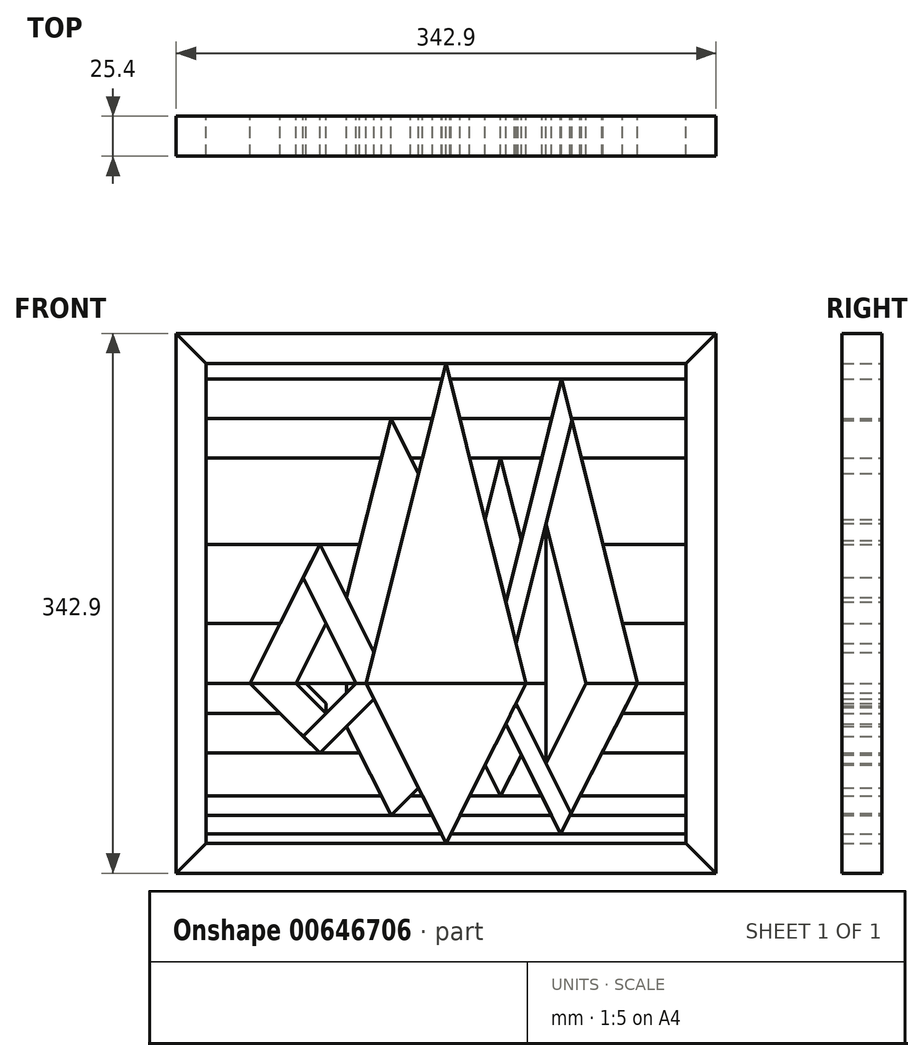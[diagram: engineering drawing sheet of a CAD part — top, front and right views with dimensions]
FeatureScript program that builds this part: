
annotation { "Feature Type Name" : "Feature", "Feature Type Description" : "" }
export const myFeature = defineFeature(function(context is Context, id is Id, definition is map)
    precondition{}
    {
        {
            var Q0;
            Q0=qCreatedBy(makeId("Front.planeOp"),FACE);
            var sketch = newSketch(context, id + "F0", { "sketchPlane" : qUnion([Q0])});
            skLineSegment(sketch, "E0.bottom", {"start": v(152.4, -152.4) * mm, "end": v(-152.4, -152.4) * mm});
            skLineSegment(sketch, "E0.top", {"start": v(152.4, 152.4) * mm, "end": v(-152.4, 152.4) * mm});
            skLineSegment(sketch, "E0.left", {"start": v(152.4, -152.4) * mm, "end": v(152.4, 152.4) * mm});
            skLineSegment(sketch, "E0.right", {"start": v(-152.4, -152.4) * mm, "end": v(-152.4, 152.4) * mm});
            skPoint(sketch, "E0.middle", {"position": v(0, 0) * mm});
            skLineSegment(sketch, "E1", {"start": v(-152.4, -50.8) * mm, "end": v(152.4, -50.8) * mm});
            skLineSegment(sketch, "E2", {"start": v(0, 152.4) * mm, "end": v(-50.8, -50.8) * mm});
            skLineSegment(sketch, "E3", {"start": v(0, 152.4) * mm, "end": v(50.8, -50.8) * mm});
            skLineSegment(sketch, "E4.MirrorCS", {"start": v(63.5, -50.8) * mm, "end": v(-7.38, -50.8) * mm});
            skLineSegment(sketch, "E5", {"start": v(79.86, 116.25) * mm, "end": v(44.45, -25.4) * mm});
            skLineSegment(sketch, "E6", {"start": v(38.1, -50.8) * mm, "end": v(63.5, -50.8) * mm});
            skLineSegment(sketch, "E7.MirrorCS", {"start": v(63.5, -50.8) * mm, "end": v(134.38, -50.8) * mm});
            skLineSegment(sketch, "E8.MirrorCS", {"start": v(88.9, -50.8) * mm, "end": v(63.5, -50.8) * mm});
            skLineSegment(sketch, "E9.MirrorCS", {"start": v(63.5, 50.8) * mm, "end": v(88.9, -50.8) * mm});
            skLineSegment(sketch, "E10", {"start": v(-76.2, -25.4) * mm, "end": v(-76.2, -50.8) * mm});
            skLineSegment(sketch, "E11", {"start": v(-76.2, -50.8) * mm, "end": v(-63.5, -50.8) * mm});
            skLineSegment(sketch, "E12.MirrorCS", {"start": v(-76.2, -50.8) * mm, "end": v(-88.9, -50.8) * mm});
            skLineSegment(sketch, "E13.MirrorCS", {"start": v(-88.9, -50.8) * mm, "end": v(-76.2, -25.4) * mm});
            skLineSegment(sketch, "E14.0", {"start": v(-124.4, -50.8) * mm, "end": v(-80.25, 37.5) * mm});
            skLineSegment(sketch, "E15.trimOffspring", {"start": v(-45.9, -31.2) * mm, "end": v(-80.25, 37.5) * mm});
            skLineSegment(sketch, "E16.trimOffspring", {"start": v(-34.96, 117.3) * mm, "end": v(-63.36, 3.7) * mm});
            skLineSegment(sketch, "E17.trimOffspring", {"start": v(34.63, 92.42) * mm, "end": v(47.72, 40.05) * mm});
            skLineSegment(sketch, "E18.0", {"start": v(73.32, 142.44) * mm, "end": v(37.9, 0.78) * mm});
            skLineSegment(sketch, "E19.0", {"start": v(73.32, 142.44) * mm, "end": v(121.63, -50.8) * mm});
            skLineSegment(sketch, "E20.0", {"start": v(-17.5, 82.39) * mm, "end": v(-34.96, 117.3) * mm});
            skLineSegment(sketch, "E21.0", {"start": v(34.63, 92.42) * mm, "end": v(24.81, 53.15) * mm});
            skLineSegment(sketch, "E22", {"start": v(-88.9, -50.8) * mm, "end": v(-76.2, -63.5) * mm});
            skLineSegment(sketch, "E23", {"start": v(-50.8, -50.8) * mm, "end": v(0, -152.4) * mm});
            skLineSegment(sketch, "E24", {"start": v(0, -152.4) * mm, "end": v(50.8, -50.8) * mm});
            skLineSegment(sketch, "E25", {"start": v(88.9, -50.8) * mm, "end": v(63.5, -101.6) * mm});
            skLineSegment(sketch, "E26", {"start": v(79.39, -133.38) * mm, "end": v(44.45, -63.5) * mm});
            skPoint(sketch, "E27.endSnap0", {"position": v(-82.55, -57.15) * mm});
            skLineSegment(sketch, "E28", {"start": v(-124.4, -50.8) * mm, "end": v(-80.25, -94.95) * mm});
            skLineSegment(sketch, "E29", {"start": v(-63.36, 3.7) * mm, "end": v(-63.36, -165.28) * mm});
            skLineSegment(sketch, "E30", {"start": v(-34.96, -134.85) * mm, "end": v(-63.36, -78.05) * mm});
            skLineSegment(sketch, "E31", {"start": v(-34.96, -134.85) * mm, "end": v(-17.5, -117.4) * mm});
            skLineSegment(sketch, "E32", {"start": v(24.81, -102.77) * mm, "end": v(34.63, -122.4) * mm});
            skLineSegment(sketch, "E33", {"start": v(34.63, -122.4) * mm, "end": v(47.72, -96.23) * mm});
            skLineSegment(sketch, "E34", {"start": v(37.9, -76.6) * mm, "end": v(72.77, -146.32) * mm});
            skLineSegment(sketch, "E35", {"start": v(121.63, -50.8) * mm, "end": v(72.77, -146.32) * mm});
            skLineSegment(sketch, "E36.trimOffspring", {"start": v(-45.9, -60.6) * mm, "end": v(-80.25, -94.95) * mm});
            skPoint(sketch, "E37.MirrorCS.start.orphan", {"position": v(-36.1, -50.8) * mm});
            skLineSegment(sketch, "E38", {"start": v(0, 152.4) * mm, "end": v(0, -50.8) * mm});
            skLineSegment(sketch, "E39", {"start": v(63.5, 50.8) * mm, "end": v(63.5, -50.8) * mm});
            skPoint(sketch, "E40", {"position": v(-101.6, 152.4) * mm});
            skPoint(sketch, "E41", {"position": v(-50.8, 152.4) * mm});
            skPoint(sketch, "E42", {"position": v(50.8, 152.4) * mm});
            skPoint(sketch, "E43", {"position": v(101.6, 152.4) * mm});
            skPoint(sketch, "E44", {"position": v(-152.4, -101.6) * mm});
            skPoint(sketch, "E45", {"position": v(-76.2, -152.4) * mm});
            skPoint(sketch, "E46", {"position": v(76.2, -152.4) * mm});
            skPoint(sketch, "E47", {"position": v(152.4, -101.6) * mm});
            skLineSegment(sketch, "E48", {"start": v(43.54, -65.31) * mm, "end": v(45.72, -66.04) * mm});
            skPoint(sketch, "E49.startSnap0", {"position": v(-25.4, 50.8) * mm});
            skLineSegment(sketch, "E50", {"start": v(-80.25, 37.5) * mm, "end": v(-152.4, 37.5) * mm});
            skLineSegment(sketch, "E51", {"start": v(-80.25, 37.5) * mm, "end": v(-54.9, 37.5) * mm});
            skLineSegment(sketch, "E52", {"start": v(99.55, 37.5) * mm, "end": v(152.4, 37.5) * mm});
            skLineSegment(sketch, "E53", {"start": v(85.82, 92.42) * mm, "end": v(152.4, 92.42) * mm});
            skLineSegment(sketch, "E54", {"start": v(-41.18, 92.42) * mm, "end": v(-152.4, 92.42) * mm});
            skLineSegment(sketch, "E55", {"start": v(-22.52, 92.42) * mm, "end": v(-15, 92.42) * mm});
            skLineSegment(sketch, "E56", {"start": v(34.63, 92.42) * mm, "end": v(15, 92.42) * mm});
            skLineSegment(sketch, "E57", {"start": v(34.63, 92.42) * mm, "end": v(60.81, 92.42) * mm});
            skLineSegment(sketch, "E58", {"start": v(73.32, 142.44) * mm, "end": v(152.4, 142.44) * mm});
            skLineSegment(sketch, "E59", {"start": v(73.32, 142.44) * mm, "end": v(2.5, 142.44) * mm});
            skLineSegment(sketch, "E60", {"start": v(-2.5, 142.44) * mm, "end": v(-152.4, 142.44) * mm});
            skLineSegment(sketch, "E61", {"start": v(152.4, 117.3) * mm, "end": v(79.6, 117.3) * mm});
            skLineSegment(sketch, "E62.trimOffspring", {"start": v(-8.78, 117.3) * mm, "end": v(-152.4, 117.3) * mm});
            skLineSegment(sketch, "E63.trimOffspring", {"start": v(67.03, 117.3) * mm, "end": v(8.78, 117.3) * mm});
            skLineSegment(sketch, "E64", {"start": v(-80.25, -94.95) * mm, "end": v(-152.4, -94.95) * mm});
            skLineSegment(sketch, "E65", {"start": v(-80.25, -94.95) * mm, "end": v(-54.9, -94.95) * mm});
            skLineSegment(sketch, "E66.trimOffspring", {"start": v(99.05, -94.95) * mm, "end": v(152.4, -94.95) * mm});
            skLineSegment(sketch, "E67", {"start": v(-152.4, -122.4) * mm, "end": v(-41.18, -122.4) * mm});
            skLineSegment(sketch, "E68.trimOffspring", {"start": v(-22.52, -122.4) * mm, "end": v(-15, -122.4) * mm});
            skLineSegment(sketch, "E69.trimOffspring", {"start": v(15, -122.4) * mm, "end": v(60.81, -122.4) * mm});
            skLineSegment(sketch, "E70.trimOffspring", {"start": v(85, -122.4) * mm, "end": v(152.4, -122.4) * mm});
            skLineSegment(sketch, "E71", {"start": v(152.4, -134.85) * mm, "end": v(78.63, -134.85) * mm});
            skLineSegment(sketch, "E72.trimOffspring", {"start": v(-8.78, -134.85) * mm, "end": v(-152.4, -134.85) * mm});
            skLineSegment(sketch, "E73.trimOffspring", {"start": v(67.03, -134.85) * mm, "end": v(8.78, -134.85) * mm});
            skLineSegment(sketch, "E74", {"start": v(-152.4, -146.32) * mm, "end": v(-3.04, -146.32) * mm});
            skLineSegment(sketch, "E75.trimOffspring", {"start": v(3.04, -146.32) * mm, "end": v(152.4, -146.32) * mm});
            skLineSegment(sketch, "E76.bottom", {"start": v(171.45, -171.45) * mm, "end": v(-171.45, -171.45) * mm});
            skLineSegment(sketch, "E76.top", {"start": v(171.45, 171.45) * mm, "end": v(-171.45, 171.45) * mm});
            skLineSegment(sketch, "E76.left", {"start": v(171.45, -171.45) * mm, "end": v(171.45, 171.45) * mm});
            skLineSegment(sketch, "E76.right", {"start": v(-171.45, -171.45) * mm, "end": v(-171.45, 171.45) * mm});
            skLineSegment(sketch, "E77", {"start": v(-152.4, 152.4) * mm, "end": v(-171.45, 171.45) * mm});
            skLineSegment(sketch, "E78", {"start": v(152.4, 152.4) * mm, "end": v(171.45, 171.45) * mm});
            skLineSegment(sketch, "E79", {"start": v(152.4, -152.4) * mm, "end": v(171.45, -171.45) * mm});
            skLineSegment(sketch, "E80", {"start": v(-152.4, -152.4) * mm, "end": v(-171.45, -171.45) * mm});
            skLineSegment(sketch, "E81", {"start": v(0, -50.8) * mm, "end": v(0, -152.4) * mm});
            skLineSegment(sketch, "E82", {"start": v(63.5, -50.8) * mm, "end": v(63.5, -101.6) * mm});
            skLineSegment(sketch, "E83", {"start": v(-76.2, -50.8) * mm, "end": v(-76.2, -63.5) * mm});
            skLineSegment(sketch, "E84", {"start": v(-76.2, -25.4) * mm, "end": v(-76.2, -12.7) * mm});
            skLineSegment(sketch, "E85", {"start": v(-76.2, -12.7) * mm, "end": v(-95.25, -50.8) * mm});
            skLineSegment(sketch, "E86", {"start": v(-76.2, -12.7) * mm, "end": v(-57.15, -50.8) * mm});
            skLineSegment(sketch, "E87", {"start": v(-76.2, -12.7) * mm, "end": v(-90.77, 16.45) * mm});
            skLineSegment(sketch, "E88", {"start": v(-95.25, -50.8) * mm, "end": v(-79.37, -66.68) * mm});
            skLineSegment(sketch, "E89", {"start": v(-79.37, -66.68) * mm, "end": v(-76.2, -69.85) * mm});
            skLineSegment(sketch, "E90", {"start": v(-76.2, -69.85) * mm, "end": v(-57.15, -50.8) * mm});
            skLineSegment(sketch, "E91", {"start": v(-76.2, -69.85) * mm, "end": v(-90.77, -84.42) * mm});
            skLineSegment(sketch, "E92", {"start": v(-76.2, -50.8) * mm, "end": v(-76.2, -69.85) * mm});
            skLineSegment(sketch, "E93", {"start": v(-152.4, -12.7) * mm, "end": v(-105.35, -12.7) * mm});
            skLineSegment(sketch, "E94.trimOffspring", {"start": v(112.1, -12.7) * mm, "end": v(152.4, -12.7) * mm});
            skLineSegment(sketch, "E95", {"start": v(-152.4, -69.85) * mm, "end": v(-105.35, -69.85) * mm});
            skLineSegment(sketch, "E96", {"start": v(111.88, -69.85) * mm, "end": v(152.4, -69.85) * mm});
            skSolve(sketch);
        }
        {
            var Q0;
            {var subQ4=sQuery(id+"F0.wireOp",EDGE,"E14.0");Q0=makeQuery(id+"F0.imprint","IMPRINT",FACE,{"disambiguationData":[TD([[makeQuery(id+"F0.imprint","IMPRINT",EDGE,{"derivedFrom":subQ4}),1.0]])]});}
            var Q1;
            {var subQ0=sQuery(id+"F0.wireOp",EDGE,"E15.trimOffspring");Q1=makeQuery(id+"F0.imprint","IMPRINT",FACE,{"disambiguationData":[TD([[makeQuery(id+"F0.imprint","IMPRINT",EDGE,{"derivedFrom":subQ0}),-1.0]])]});}
            var Q2;
            {var subQ3=sQuery(id+"F0.wireOp",EDGE,"E52");Q2=makeQuery(id+"F0.imprint","IMPRINT",FACE,{"disambiguationData":[TD([[makeQuery(id+"F0.imprint","IMPRINT",EDGE,{"derivedFrom":subQ3}),-1.0]])]});}
            extrude(context, id + "F1", {"entities" : qUnion([Q0, Q1, Q2]), "depth" : 25.4 * mm, "offsetDistance" : 25.4 * mm});
        }
        {
            var Q0;
            {var subQ3=sQuery(id+"F0.wireOp",EDGE,"E5");Q0=makeQuery(id+"F0.imprint","IMPRINT",FACE,{"disambiguationData":[TD([[makeQuery(id+"F0.imprint","IMPRINT",EDGE,{"derivedFrom":subQ3}),1.0]])]});}
            var Q1;
            Q1=makeQuery(id+"F0.imprint","IMPRINT",FACE,{"disambiguationData":[TD([[makeQuery(id+"F0.imprint","IMPRINT",EDGE,{"derivedFrom":sQuery(id+"F0.wireOp",EDGE,"E8.MirrorCS")}),-1.0]])]});
            extrude(context, id + "F2", {"entities" : qUnion([Q0, Q1]), "depth" : 25.4 * mm, "offsetDistance" : 25.4 * mm});
        }
        {
            var Q0;
            {var subQ0=sQuery(id+"F0.wireOp",EDGE,"E50");Q0=makeQuery(id+"F0.imprint","IMPRINT",FACE,{"disambiguationData":[TD([[makeQuery(id+"F0.imprint","IMPRINT",EDGE,{"derivedFrom":subQ0}),-1.0]])]});}
            var Q1;
            {var subQ3=sQuery(id+"F0.wireOp",EDGE,"E55");Q1=makeQuery(id+"F0.imprint","IMPRINT",FACE,{"disambiguationData":[TD([[makeQuery(id+"F0.imprint","IMPRINT",EDGE,{"derivedFrom":subQ3}),-1.0]])]});}
            var Q2;
            {var subQ0=sQuery(id+"F0.wireOp",EDGE,"E21.0");Q2=makeQuery(id+"F0.imprint","IMPRINT",FACE,{"disambiguationData":[TD([[makeQuery(id+"F0.imprint","IMPRINT",EDGE,{"derivedFrom":subQ0}),-1.0]])]});}
            var Q3;
            {var subQ0=sQuery(id+"F0.wireOp",EDGE,"E17.trimOffspring");Q3=makeQuery(id+"F0.imprint","IMPRINT",FACE,{"disambiguationData":[TD([[makeQuery(id+"F0.imprint","IMPRINT",EDGE,{"derivedFrom":subQ0}),1.0]])]});}
            var Q4;
            {var subQ0=sQuery(id+"F0.wireOp",EDGE,"E52");Q4=makeQuery(id+"F0.imprint","IMPRINT",FACE,{"disambiguationData":[TD([[makeQuery(id+"F0.imprint","IMPRINT",EDGE,{"derivedFrom":subQ0}),1.0]])]});}
            extrude(context, id + "F3", {"entities" : qUnion([Q0, Q1, Q2, Q3, Q4]), "depth" : 25.4 * mm, "offsetDistance" : 25.4 * mm});
        }
        {
            var Q0;
            {var subQ0=sQuery(id+"F0.wireOp",EDGE,"E54");Q0=makeQuery(id+"F0.imprint","IMPRINT",FACE,{"disambiguationData":[TD([[makeQuery(id+"F0.imprint","IMPRINT",EDGE,{"derivedFrom":subQ0}),-1.0]])]});}
            var Q1;
            {var subQ0=sQuery(id+"F0.wireOp",EDGE,"E55");Q1=makeQuery(id+"F0.imprint","IMPRINT",FACE,{"disambiguationData":[TD([[makeQuery(id+"F0.imprint","IMPRINT",EDGE,{"derivedFrom":subQ0}),1.0]])]});}
            var Q2;
            {var subQ1=sQuery(id+"F0.wireOp",EDGE,"E56");Q2=makeQuery(id+"F0.imprint","IMPRINT",FACE,{"disambiguationData":[TD([[makeQuery(id+"F0.imprint","IMPRINT",EDGE,{"derivedFrom":subQ1}),-1.0]])]});}
            var Q3;
            {var subQ0=sQuery(id+"F0.wireOp",EDGE,"E53");Q3=makeQuery(id+"F0.imprint","IMPRINT",FACE,{"disambiguationData":[TD([[makeQuery(id+"F0.imprint","IMPRINT",EDGE,{"derivedFrom":subQ0}),1.0]])]});}
            extrude(context, id + "F4", {"entities" : qUnion([Q0, Q1, Q2, Q3]), "depth" : 25.4 * mm, "offsetDistance" : 25.4 * mm});
        }
        {
            var Q0;
            {var subQ0=sQuery(id+"F0.wireOp",EDGE,"E60");Q0=makeQuery(id+"F0.imprint","IMPRINT",FACE,{"disambiguationData":[TD([[makeQuery(id+"F0.imprint","IMPRINT",EDGE,{"derivedFrom":subQ0}),1.0]])]});}
            var Q1;
            {var subQ0=sQuery(id+"F0.wireOp",EDGE,"E59");Q1=makeQuery(id+"F0.imprint","IMPRINT",FACE,{"disambiguationData":[TD([[makeQuery(id+"F0.imprint","IMPRINT",EDGE,{"derivedFrom":subQ0}),1.0]])]});}
            var Q2;
            {var subQ0=sQuery(id+"F0.wireOp",EDGE,"E58");Q2=makeQuery(id+"F0.imprint","IMPRINT",FACE,{"disambiguationData":[TD([[makeQuery(id+"F0.imprint","IMPRINT",EDGE,{"derivedFrom":subQ0}),-1.0]])]});}
            extrude(context, id + "F5", {"entities" : qUnion([Q0, Q1, Q2]), "depth" : 25.4 * mm, "offsetDistance" : 25.4 * mm});
        }
        {
            var Q0;
            {var subQ5=sQuery(id+"F0.wireOp",EDGE,"E60");Q0=makeQuery(id+"F0.imprint","IMPRINT",FACE,{"disambiguationData":[TD([[makeQuery(id+"F0.imprint","IMPRINT",EDGE,{"derivedFrom":subQ5}),-1.0]])]});}
            var Q1;
            {var subQ6=sQuery(id+"F0.wireOp",EDGE,"E58");Q1=makeQuery(id+"F0.imprint","IMPRINT",FACE,{"disambiguationData":[TD([[makeQuery(id+"F0.imprint","IMPRINT",EDGE,{"derivedFrom":subQ6}),1.0]])]});}
            extrude(context, id + "F6", {"entities" : qUnion([Q0, Q1]), "depth" : 25.4 * mm, "offsetDistance" : 25.4 * mm});
        }
        {
            var Q0;
            {var subQ4=sQuery(id+"F0.wireOp",EDGE,"E28");Q0=makeQuery(id+"F0.imprint","IMPRINT",FACE,{"disambiguationData":[TD([[makeQuery(id+"F0.imprint","IMPRINT",EDGE,{"derivedFrom":subQ4}),-1.0]])]});}
            var Q1;
            {var subQ0=sQuery(id+"F0.wireOp",EDGE,"E36.trimOffspring");Q1=makeQuery(id+"F0.imprint","IMPRINT",FACE,{"disambiguationData":[TD([[makeQuery(id+"F0.imprint","IMPRINT",EDGE,{"derivedFrom":subQ0}),1.0]])]});}
            var Q2;
            {var subQ0=sQuery(id+"F0.wireOp",EDGE,"E30");var subQ3=sQuery(id+"F0.wireOp",EDGE,"E65");var subQ5=makeQuery(id+"F0.imprint","INTERSECT",VERTEX,{"derivedFrom":[subQ0,subQ3]});Q2=makeQuery(id+"F0.imprint","IMPRINT",FACE,{"disambiguationData":[TD([[makeQuery(id+"F0.imprint","IMPRINT",EDGE,{"disambiguationData":[TD([[subQ5,1.0]])],"derivedFrom":subQ3}),1.0]])]});}
            var Q3;
            {var subQ3=sQuery(id+"F0.wireOp",EDGE,"E66.trimOffspring");Q3=makeQuery(id+"F0.imprint","IMPRINT",FACE,{"disambiguationData":[TD([[makeQuery(id+"F0.imprint","IMPRINT",EDGE,{"derivedFrom":subQ3}),1.0]])]});}
            extrude(context, id + "F7", {"entities" : qUnion([Q0, Q1, Q2, Q3]), "depth" : 25.4 * mm, "offsetDistance" : 25.4 * mm});
        }
        {
            var Q0;
            {var subQ1=sQuery(id+"F0.wireOp",EDGE,"E64");Q0=makeQuery(id+"F0.imprint","IMPRINT",FACE,{"disambiguationData":[TD([[makeQuery(id+"F0.imprint","IMPRINT",EDGE,{"derivedFrom":subQ1}),1.0]])]});}
            var Q1;
            {var subQ0=sQuery(id+"F0.wireOp",EDGE,"E65");var subQ1=sQuery(id+"F0.wireOp",EDGE,"E29");var subQ2=makeQuery(id+"F0.imprint","INTERSECT",VERTEX,{"derivedFrom":[subQ1,subQ0]});Q1=makeQuery(id+"F0.imprint","IMPRINT",FACE,{"disambiguationData":[TD([[makeQuery(id+"F0.imprint","IMPRINT",EDGE,{"disambiguationData":[TD([[subQ2,-1.0]])],"derivedFrom":subQ1}),1.0]])]});}
            var Q2;
            {var subQ3=sQuery(id+"F0.wireOp",EDGE,"E68.trimOffspring");Q2=makeQuery(id+"F0.imprint","IMPRINT",FACE,{"disambiguationData":[TD([[makeQuery(id+"F0.imprint","IMPRINT",EDGE,{"derivedFrom":subQ3}),1.0]])]});}
            var Q3;
            {var subQ0=sQuery(id+"F0.wireOp",EDGE,"E32");Q3=makeQuery(id+"F0.imprint","IMPRINT",FACE,{"disambiguationData":[TD([[makeQuery(id+"F0.imprint","IMPRINT",EDGE,{"derivedFrom":subQ0}),-1.0]])]});}
            var Q4;
            {var subQ0=sQuery(id+"F0.wireOp",EDGE,"E33");Q4=makeQuery(id+"F0.imprint","IMPRINT",FACE,{"disambiguationData":[TD([[makeQuery(id+"F0.imprint","IMPRINT",EDGE,{"derivedFrom":subQ0}),-1.0]])]});}
            var Q5;
            {var subQ0=sQuery(id+"F0.wireOp",EDGE,"E66.trimOffspring");Q5=makeQuery(id+"F0.imprint","IMPRINT",FACE,{"disambiguationData":[TD([[makeQuery(id+"F0.imprint","IMPRINT",EDGE,{"derivedFrom":subQ0}),-1.0]])]});}
            extrude(context, id + "F8", {"entities" : qUnion([Q0, Q1, Q2, Q3, Q4, Q5]), "depth" : 25.4 * mm, "offsetDistance" : 25.4 * mm});
        }
        {
            var Q0;
            {var subQ0=sQuery(id+"F0.wireOp",EDGE,"E67");var subQ1=sQuery(id+"F0.wireOp",EDGE,"E0.right");var subQ2=makeQuery(id+"F0.imprint","INTERSECT",VERTEX,{"derivedFrom":[subQ1,subQ0]});Q0=makeQuery(id+"F0.imprint","IMPRINT",FACE,{"disambiguationData":[TD([[makeQuery(id+"F0.imprint","IMPRINT",EDGE,{"disambiguationData":[TD([[subQ2,1.0]])],"derivedFrom":subQ1}),-1.0]])]});}
            var Q1;
            {var subQ0=sQuery(id+"F0.wireOp",EDGE,"E67");var subQ1=sQuery(id+"F0.wireOp",EDGE,"E29");var subQ2=makeQuery(id+"F0.imprint","INTERSECT",VERTEX,{"derivedFrom":[subQ1,subQ0]});Q1=makeQuery(id+"F0.imprint","IMPRINT",FACE,{"disambiguationData":[TD([[makeQuery(id+"F0.imprint","IMPRINT",EDGE,{"disambiguationData":[TD([[subQ2,-1.0]])],"derivedFrom":subQ1}),1.0]])]});}
            var Q2;
            {var subQ0=sQuery(id+"F0.wireOp",EDGE,"E68.trimOffspring");Q2=makeQuery(id+"F0.imprint","IMPRINT",FACE,{"disambiguationData":[TD([[makeQuery(id+"F0.imprint","IMPRINT",EDGE,{"derivedFrom":subQ0}),-1.0]])]});}
            var Q3;
            {var subQ4=sQuery(id+"F0.wireOp",EDGE,"E73.trimOffspring");Q3=makeQuery(id+"F0.imprint","IMPRINT",FACE,{"disambiguationData":[TD([[makeQuery(id+"F0.imprint","IMPRINT",EDGE,{"derivedFrom":subQ4}),-1.0]])]});}
            var Q4;
            {var subQ0=sQuery(id+"F0.wireOp",EDGE,"E70.trimOffspring");Q4=makeQuery(id+"F0.imprint","IMPRINT",FACE,{"disambiguationData":[TD([[makeQuery(id+"F0.imprint","IMPRINT",EDGE,{"derivedFrom":subQ0}),-1.0]])]});}
            extrude(context, id + "F9", {"entities" : qUnion([Q0, Q1, Q2, Q3, Q4]), "depth" : 25.4 * mm, "offsetDistance" : 25.4 * mm});
        }
        {
            var Q0;
            {var subQ0=sQuery(id+"F0.wireOp",EDGE,"E72.trimOffspring");var subQ1=sQuery(id+"F0.wireOp",EDGE,"E0.right");var subQ2=makeQuery(id+"F0.imprint","INTERSECT",VERTEX,{"derivedFrom":[subQ1,subQ0]});Q0=makeQuery(id+"F0.imprint","IMPRINT",FACE,{"disambiguationData":[TD([[makeQuery(id+"F0.imprint","IMPRINT",EDGE,{"disambiguationData":[TD([[subQ2,1.0]])],"derivedFrom":subQ1}),-1.0]])]});}
            var Q1;
            {var subQ0=sQuery(id+"F0.wireOp",EDGE,"E72.trimOffspring");var subQ2=sQuery(id+"F0.wireOp",EDGE,"E23");var subQ3=makeQuery(id+"F0.imprint","INTERSECT",VERTEX,{"derivedFrom":[subQ2,subQ0]});Q1=makeQuery(id+"F0.imprint","IMPRINT",FACE,{"disambiguationData":[TD([[makeQuery(id+"F0.imprint","IMPRINT",EDGE,{"disambiguationData":[TD([[subQ3,-1.0]])],"derivedFrom":subQ2}),-1.0]])]});}
            var Q2;
            {var subQ0=sQuery(id+"F0.wireOp",EDGE,"E73.trimOffspring");Q2=makeQuery(id+"F0.imprint","IMPRINT",FACE,{"disambiguationData":[TD([[makeQuery(id+"F0.imprint","IMPRINT",EDGE,{"derivedFrom":subQ0}),1.0]])]});}
            var Q3;
            {var subQ0=sQuery(id+"F0.wireOp",EDGE,"E71");Q3=makeQuery(id+"F0.imprint","IMPRINT",FACE,{"disambiguationData":[TD([[makeQuery(id+"F0.imprint","IMPRINT",EDGE,{"derivedFrom":subQ0}),1.0]])]});}
            extrude(context, id + "F10", {"entities" : qUnion([Q0, Q1, Q2, Q3]), "depth" : 25.4 * mm, "offsetDistance" : 25.4 * mm});
        }
        {
            var Q0;
            {var subQ0=sQuery(id+"F0.wireOp",EDGE,"E0.right");var subQ1=sQuery(id+"F0.wireOp",EDGE,"E0.bottom");var subQ2=makeQuery(id+"F0.imprint","INTERSECT",VERTEX,{"derivedFrom":[subQ1,subQ0]});Q0=makeQuery(id+"F0.imprint","IMPRINT",FACE,{"disambiguationData":[TD([[makeQuery(id+"F0.imprint","IMPRINT",EDGE,{"disambiguationData":[TD([[subQ2,1.0]])],"derivedFrom":subQ1}),-1.0]])]});}
            var Q1;
            {var subQ1=sQuery(id+"F0.wireOp",EDGE,"E0.bottom");var subQ3=sQuery(id+"F0.wireOp",EDGE,"E29");var subQ4=makeQuery(id+"F0.imprint","INTERSECT",VERTEX,{"derivedFrom":[subQ1,subQ3]});Q1=makeQuery(id+"F0.imprint","IMPRINT",FACE,{"disambiguationData":[TD([[makeQuery(id+"F0.imprint","IMPRINT",EDGE,{"disambiguationData":[TD([[subQ4,1.0]])],"derivedFrom":subQ3}),1.0]])]});}
            var Q2;
            {var subQ4=sQuery(id+"F0.wireOp",EDGE,"E0.bottom");var subQ6=sQuery(id+"F0.wireOp",EDGE,"E0.left");var subQ7=makeQuery(id+"F0.imprint","INTERSECT",VERTEX,{"derivedFrom":[subQ4,subQ6]});Q2=makeQuery(id+"F0.imprint","IMPRINT",FACE,{"disambiguationData":[TD([[makeQuery(id+"F0.imprint","IMPRINT",EDGE,{"disambiguationData":[TD([[subQ7,-1.0]])],"derivedFrom":subQ6}),1.0]])]});}
            extrude(context, id + "F11", {"entities" : qUnion([Q0, Q1, Q2]), "depth" : 25.4 * mm, "offsetDistance" : 25.4 * mm});
        }
        {
            var Q0;
            Q0=makeQuery(id+"F0.imprint","IMPRINT",FACE,{"disambiguationData":[TD([[makeQuery(id+"F0.imprint","IMPRINT",EDGE,{"derivedFrom":sQuery(id+"F0.wireOp",EDGE,"E76.right")}),-1.0]])]});
            extrude(context, id + "F12", {"entities" : qUnion([Q0]), "depth" : 25.4 * mm, "offsetDistance" : 25.4 * mm});
        }
        {
            var Q0;
            Q0=makeQuery(id+"F0.imprint","IMPRINT",FACE,{"disambiguationData":[TD([[makeQuery(id+"F0.imprint","IMPRINT",EDGE,{"derivedFrom":sQuery(id+"F0.wireOp",EDGE,"E76.top")}),1.0]])]});
            extrude(context, id + "F13", {"entities" : qUnion([Q0]), "depth" : 25.4 * mm, "offsetDistance" : 25.4 * mm});
        }
        {
            var Q0;
            Q0=makeQuery(id+"F0.imprint","IMPRINT",FACE,{"disambiguationData":[TD([[makeQuery(id+"F0.imprint","IMPRINT",EDGE,{"derivedFrom":sQuery(id+"F0.wireOp",EDGE,"E76.left")}),1.0]])]});
            extrude(context, id + "F14", {"entities" : qUnion([Q0]), "depth" : 25.4 * mm, "offsetDistance" : 25.4 * mm});
        }
        {
            var Q0;
            Q0=makeQuery(id+"F0.imprint","IMPRINT",FACE,{"disambiguationData":[TD([[makeQuery(id+"F0.imprint","IMPRINT",EDGE,{"derivedFrom":sQuery(id+"F0.wireOp",EDGE,"E76.bottom")}),-1.0]])]});
            extrude(context, id + "F15", {"entities" : qUnion([Q0]), "depth" : 25.4 * mm, "offsetDistance" : 25.4 * mm});
        }
        {
            var Q0;
            {var subQ6=sQuery(id+"F0.wireOp",EDGE,"E81");Q0=makeQuery(id+"F0.imprint","IMPRINT",FACE,{"disambiguationData":[TD([[makeQuery(id+"F0.imprint","IMPRINT",EDGE,{"derivedFrom":subQ6}),-1.0]])]});}
            var Q1;
            {var subQ10=sQuery(id+"F0.wireOp",EDGE,"E81");Q1=makeQuery(id+"F0.imprint","IMPRINT",FACE,{"disambiguationData":[TD([[makeQuery(id+"F0.imprint","IMPRINT",EDGE,{"derivedFrom":subQ10}),1.0]])]});}
            extrude(context, id + "F16", {"entities" : qUnion([Q0, Q1]), "depth" : 25.4 * mm, "offsetDistance" : 25.4 * mm});
        }
        {
            var Q0;
            {var subQ4=sQuery(id+"F0.wireOp",EDGE,"E82");Q0=makeQuery(id+"F0.imprint","IMPRINT",FACE,{"disambiguationData":[TD([[makeQuery(id+"F0.imprint","IMPRINT",EDGE,{"derivedFrom":subQ4}),-1.0]])]});}
            var Q1;
            Q1=makeQuery(id+"F0.imprint","IMPRINT",FACE,{"disambiguationData":[TD([[makeQuery(id+"F0.imprint","IMPRINT",EDGE,{"derivedFrom":sQuery(id+"F0.wireOp",EDGE,"E8.MirrorCS")}),1.0]])]});
            extrude(context, id + "F17", {"entities" : qUnion([Q0, Q1]), "depth" : 25.4 * mm, "offsetDistance" : 25.4 * mm});
        }
        {
            var Q0;
            {var subQ4=sQuery(id+"F0.wireOp",EDGE,"E15.trimOffspring");var subQ5=sQuery(id+"F0.wireOp",EDGE,"E2");var subQ6=makeQuery(id+"F0.imprint","INTERSECT",VERTEX,{"derivedFrom":[subQ5,subQ4]});Q0=makeQuery(id+"F0.imprint","IMPRINT",FACE,{"disambiguationData":[TD([[makeQuery(id+"F0.imprint","IMPRINT",EDGE,{"disambiguationData":[TD([[subQ6,1.0]])],"derivedFrom":subQ5}),-1.0]])]});}
            extrude(context, id + "F18", {"entities" : qUnion([Q0]), "depth" : 25.4 * mm, "offsetDistance" : 25.4 * mm});
        }
        {
            var Q0;
            {var subQ4=sQuery(id+"F0.wireOp",EDGE,"E17.trimOffspring");Q0=makeQuery(id+"F0.imprint","IMPRINT",FACE,{"disambiguationData":[TD([[makeQuery(id+"F0.imprint","IMPRINT",EDGE,{"derivedFrom":subQ4}),-1.0]])]});}
            extrude(context, id + "F19", {"entities" : qUnion([Q0]), "depth" : 25.4 * mm, "offsetDistance" : 25.4 * mm});
        }
        {
            var Q0;
            {var subQ4=sQuery(id+"F0.wireOp",EDGE,"E5");var subQ7=sQuery(id+"F0.wireOp",EDGE,"E3");var subQ8=makeQuery(id+"F0.imprint","INTERSECT",VERTEX,{"derivedFrom":[subQ7,subQ4]});Q0=makeQuery(id+"F0.imprint","IMPRINT",FACE,{"disambiguationData":[TD([[makeQuery(id+"F0.imprint","IMPRINT",EDGE,{"disambiguationData":[TD([[subQ8,1.0]])],"derivedFrom":subQ7}),1.0]])]});}
            extrude(context, id + "F20", {"entities" : qUnion([Q0]), "depth" : 25.4 * mm, "offsetDistance" : 25.4 * mm});
        }
        {
            var Q0;
            {var subQ4=sQuery(id+"F0.wireOp",EDGE,"E9.MirrorCS");Q0=makeQuery(id+"F0.imprint","IMPRINT",FACE,{"disambiguationData":[TD([[makeQuery(id+"F0.imprint","IMPRINT",EDGE,{"derivedFrom":subQ4}),1.0]])]});}
            extrude(context, id + "F21", {"entities" : qUnion([Q0]), "depth" : 25.4 * mm, "offsetDistance" : 25.4 * mm});
        }
        {
            var Q0;
            {var subQ5=sQuery(id+"F0.wireOp",EDGE,"E31");var subQ7=sQuery(id+"F0.wireOp",EDGE,"E23");var subQ8=makeQuery(id+"F0.imprint","INTERSECT",VERTEX,{"derivedFrom":[subQ7,subQ5]});Q0=makeQuery(id+"F0.imprint","IMPRINT",FACE,{"disambiguationData":[TD([[makeQuery(id+"F0.imprint","IMPRINT",EDGE,{"disambiguationData":[TD([[subQ8,1.0]])],"derivedFrom":subQ7}),-1.0]])]});}
            extrude(context, id + "F22", {"entities" : qUnion([Q0]), "depth" : 25.4 * mm, "offsetDistance" : 25.4 * mm});
        }
        {
            var Q0;
            {var subQ0=sQuery(id+"F0.wireOp",EDGE,"E32");Q0=makeQuery(id+"F0.imprint","IMPRINT",FACE,{"disambiguationData":[TD([[makeQuery(id+"F0.imprint","IMPRINT",EDGE,{"derivedFrom":subQ0}),1.0]])]});}
            extrude(context, id + "F23", {"entities" : qUnion([Q0]), "depth" : 25.4 * mm, "offsetDistance" : 25.4 * mm});
        }
        {
            var Q0;
            {var subQ10=sQuery(id+"F0.wireOp",EDGE,"E48");Q0=makeQuery(id+"F0.imprint","IMPRINT",FACE,{"disambiguationData":[TD([[makeQuery(id+"F0.imprint","IMPRINT",EDGE,{"derivedFrom":subQ10}),-1.0]])]});}
            extrude(context, id + "F24", {"entities" : qUnion([Q0]), "depth" : 25.4 * mm, "offsetDistance" : 25.4 * mm});
        }
        {
            var Q0;
            {var subQ5=sQuery(id+"F0.wireOp",EDGE,"E25");Q0=makeQuery(id+"F0.imprint","IMPRINT",FACE,{"disambiguationData":[TD([[makeQuery(id+"F0.imprint","IMPRINT",EDGE,{"derivedFrom":subQ5}),1.0]])]});}
            extrude(context, id + "F25", {"entities" : qUnion([Q0]), "depth" : 25.4 * mm, "offsetDistance" : 25.4 * mm});
        }
        {
            var Q0;
            Q0=makeQuery(id+"F0.imprint","IMPRINT",FACE,{"disambiguationData":[TD([[makeQuery(id+"F0.imprint","IMPRINT",EDGE,{"derivedFrom":sQuery(id+"F0.wireOp",EDGE,"E10")}),-1.0]])]});
            var Q1;
            {var subQ0=sQuery(id+"F0.wireOp",EDGE,"E13.MirrorCS");Q1=makeQuery(id+"F0.imprint","IMPRINT",FACE,{"disambiguationData":[TD([[makeQuery(id+"F0.imprint","IMPRINT",EDGE,{"derivedFrom":subQ0}),1.0]])]});}
            var Q2;
            Q2=makeQuery(id+"F0.imprint","IMPRINT",FACE,{"disambiguationData":[TD([[makeQuery(id+"F0.imprint","IMPRINT",EDGE,{"derivedFrom":sQuery(id+"F0.wireOp",EDGE,"E10")}),1.0]])]});
            var Q3;
            {var subQ1=sQuery(id+"F0.wireOp",EDGE,"E1");var subQ3=sQuery(id+"F0.wireOp",EDGE,"E29");var subQ4=makeQuery(id+"F0.imprint","INTERSECT",VERTEX,{"derivedFrom":[subQ1,subQ3]});Q3=makeQuery(id+"F0.imprint","IMPRINT",FACE,{"disambiguationData":[TD([[makeQuery(id+"F0.imprint","IMPRINT",EDGE,{"disambiguationData":[TD([[subQ4,1.0]])],"derivedFrom":subQ3}),1.0]])]});}
            extrude(context, id + "F26", {"entities" : qUnion([Q0, Q1, Q2, Q3]), "depth" : 25.4 * mm, "offsetDistance" : 25.4 * mm});
        }
        {
            var Q0;
            {var subQ1=sQuery(id+"F0.wireOp",EDGE,"E15.trimOffspring");var subQ5=sQuery(id+"F0.wireOp",EDGE,"E2");var subQ6=makeQuery(id+"F0.imprint","INTERSECT",VERTEX,{"derivedFrom":[subQ5,subQ1]});Q0=makeQuery(id+"F0.imprint","IMPRINT",FACE,{"disambiguationData":[TD([[makeQuery(id+"F0.imprint","IMPRINT",EDGE,{"disambiguationData":[TD([[subQ6,-1.0]])],"derivedFrom":subQ5}),-1.0]])]});}
            var Q1;
            {var subQ0=sQuery(id+"F0.wireOp",EDGE,"E87");Q1=makeQuery(id+"F0.imprint","IMPRINT",FACE,{"disambiguationData":[TD([[makeQuery(id+"F0.imprint","IMPRINT",EDGE,{"derivedFrom":subQ0}),-1.0]])]});}
            extrude(context, id + "F27", {"entities" : qUnion([Q0, Q1]), "depth" : 25.4 * mm, "offsetDistance" : 25.4 * mm});
        }
        {
            var Q0;
            {var subQ3=sQuery(id+"F0.wireOp",EDGE,"E85");Q0=makeQuery(id+"F0.imprint","IMPRINT",FACE,{"disambiguationData":[TD([[makeQuery(id+"F0.imprint","IMPRINT",EDGE,{"derivedFrom":subQ3}),-1.0]])]});}
            extrude(context, id + "F28", {"entities" : qUnion([Q0]), "depth" : 25.4 * mm, "offsetDistance" : 25.4 * mm});
        }
        {
            var Q0;
            {var subQ4=sQuery(id+"F0.wireOp",EDGE,"E88");Q0=makeQuery(id+"F0.imprint","IMPRINT",FACE,{"disambiguationData":[TD([[makeQuery(id+"F0.imprint","IMPRINT",EDGE,{"derivedFrom":subQ4}),-1.0]])]});}
            extrude(context, id + "F29", {"entities" : qUnion([Q0]), "depth" : 25.4 * mm, "offsetDistance" : 25.4 * mm});
        }
        {
            var Q0;
            {var subQ0=sQuery(id+"F0.wireOp",EDGE,"E91");Q0=makeQuery(id+"F0.imprint","IMPRINT",FACE,{"disambiguationData":[TD([[makeQuery(id+"F0.imprint","IMPRINT",EDGE,{"derivedFrom":subQ0}),1.0]])]});}
            var Q1;
            {var subQ0=sQuery(id+"F0.wireOp",EDGE,"E36.trimOffspring");var subQ5=sQuery(id+"F0.wireOp",EDGE,"E23");var subQ6=makeQuery(id+"F0.imprint","INTERSECT",VERTEX,{"derivedFrom":[subQ5,subQ0]});Q1=makeQuery(id+"F0.imprint","IMPRINT",FACE,{"disambiguationData":[TD([[makeQuery(id+"F0.imprint","IMPRINT",EDGE,{"disambiguationData":[TD([[subQ6,1.0]])],"derivedFrom":subQ5}),-1.0]])]});}
            extrude(context, id + "F30", {"entities" : qUnion([Q0, Q1]), "depth" : 25.4 * mm, "offsetDistance" : 25.4 * mm});
        }
        {
            var Q0;
            {var subQ0=sQuery(id+"F0.wireOp",EDGE,"E12.MirrorCS");Q0=makeQuery(id+"F0.imprint","IMPRINT",FACE,{"disambiguationData":[TD([[makeQuery(id+"F0.imprint","IMPRINT",EDGE,{"derivedFrom":subQ0}),1.0]])]});}
            var Q1;
            {var subQ1=sQuery(id+"F0.wireOp",EDGE,"E22");Q1=makeQuery(id+"F0.imprint","IMPRINT",FACE,{"disambiguationData":[TD([[makeQuery(id+"F0.imprint","IMPRINT",EDGE,{"derivedFrom":subQ1}),-1.0]])]});}
            var Q2;
            {var subQ7=sQuery(id+"F0.wireOp",EDGE,"E11");Q2=makeQuery(id+"F0.imprint","IMPRINT",FACE,{"disambiguationData":[TD([[makeQuery(id+"F0.imprint","IMPRINT",EDGE,{"derivedFrom":subQ7}),-1.0]])]});}
            var Q3;
            {var subQ1=sQuery(id+"F0.wireOp",EDGE,"E1");var subQ3=sQuery(id+"F0.wireOp",EDGE,"E29");var subQ4=makeQuery(id+"F0.imprint","INTERSECT",VERTEX,{"derivedFrom":[subQ1,subQ3]});Q3=makeQuery(id+"F0.imprint","IMPRINT",FACE,{"disambiguationData":[TD([[makeQuery(id+"F0.imprint","IMPRINT",EDGE,{"disambiguationData":[TD([[subQ4,-1.0]])],"derivedFrom":subQ3}),1.0]])]});}
            extrude(context, id + "F31", {"entities" : qUnion([Q0, Q1, Q2, Q3]), "depth" : 25.4 * mm, "offsetDistance" : 25.4 * mm});
        }
        {
            var Q0;
            {var subQ3=sQuery(id+"F0.wireOp",EDGE,"E93");Q0=makeQuery(id+"F0.imprint","IMPRINT",FACE,{"disambiguationData":[TD([[makeQuery(id+"F0.imprint","IMPRINT",EDGE,{"derivedFrom":subQ3}),-1.0]])]});}
            var Q1;
            {var subQ3=sQuery(id+"F0.wireOp",EDGE,"E94.trimOffspring");Q1=makeQuery(id+"F0.imprint","IMPRINT",FACE,{"disambiguationData":[TD([[makeQuery(id+"F0.imprint","IMPRINT",EDGE,{"derivedFrom":subQ3}),-1.0]])]});}
            extrude(context, id + "F32", {"entities" : qUnion([Q0, Q1]), "depth" : 25.4 * mm, "offsetDistance" : 25.4 * mm});
        }
        {
            var Q0;
            {var subQ3=sQuery(id+"F0.wireOp",EDGE,"E95");Q0=makeQuery(id+"F0.imprint","IMPRINT",FACE,{"disambiguationData":[TD([[makeQuery(id+"F0.imprint","IMPRINT",EDGE,{"derivedFrom":subQ3}),1.0]])]});}
            var Q1;
            {var subQ3=sQuery(id+"F0.wireOp",EDGE,"E96");Q1=makeQuery(id+"F0.imprint","IMPRINT",FACE,{"disambiguationData":[TD([[makeQuery(id+"F0.imprint","IMPRINT",EDGE,{"derivedFrom":subQ3}),1.0]])]});}
            extrude(context, id + "F33", {"entities" : qUnion([Q0, Q1]), "depth" : 25.4 * mm, "offsetDistance" : 25.4 * mm});
        }
        {
            var Q0;
            {var subQ4=sQuery(id+"F0.wireOp",EDGE,"E38");Q0=makeQuery(id+"F0.imprint","IMPRINT",FACE,{"disambiguationData":[TD([[makeQuery(id+"F0.imprint","IMPRINT",EDGE,{"derivedFrom":subQ4}),-1.0]])]});}
            var Q1;
            {var subQ5=sQuery(id+"F0.wireOp",EDGE,"E38");Q1=makeQuery(id+"F0.imprint","IMPRINT",FACE,{"disambiguationData":[TD([[makeQuery(id+"F0.imprint","IMPRINT",EDGE,{"derivedFrom":subQ5}),1.0]])]});}
            extrude(context, id + "F34", {"entities" : qUnion([Q0, Q1]), "depth" : 25.4 * mm, "offsetDistance" : 25.4 * mm});
        }
    });
